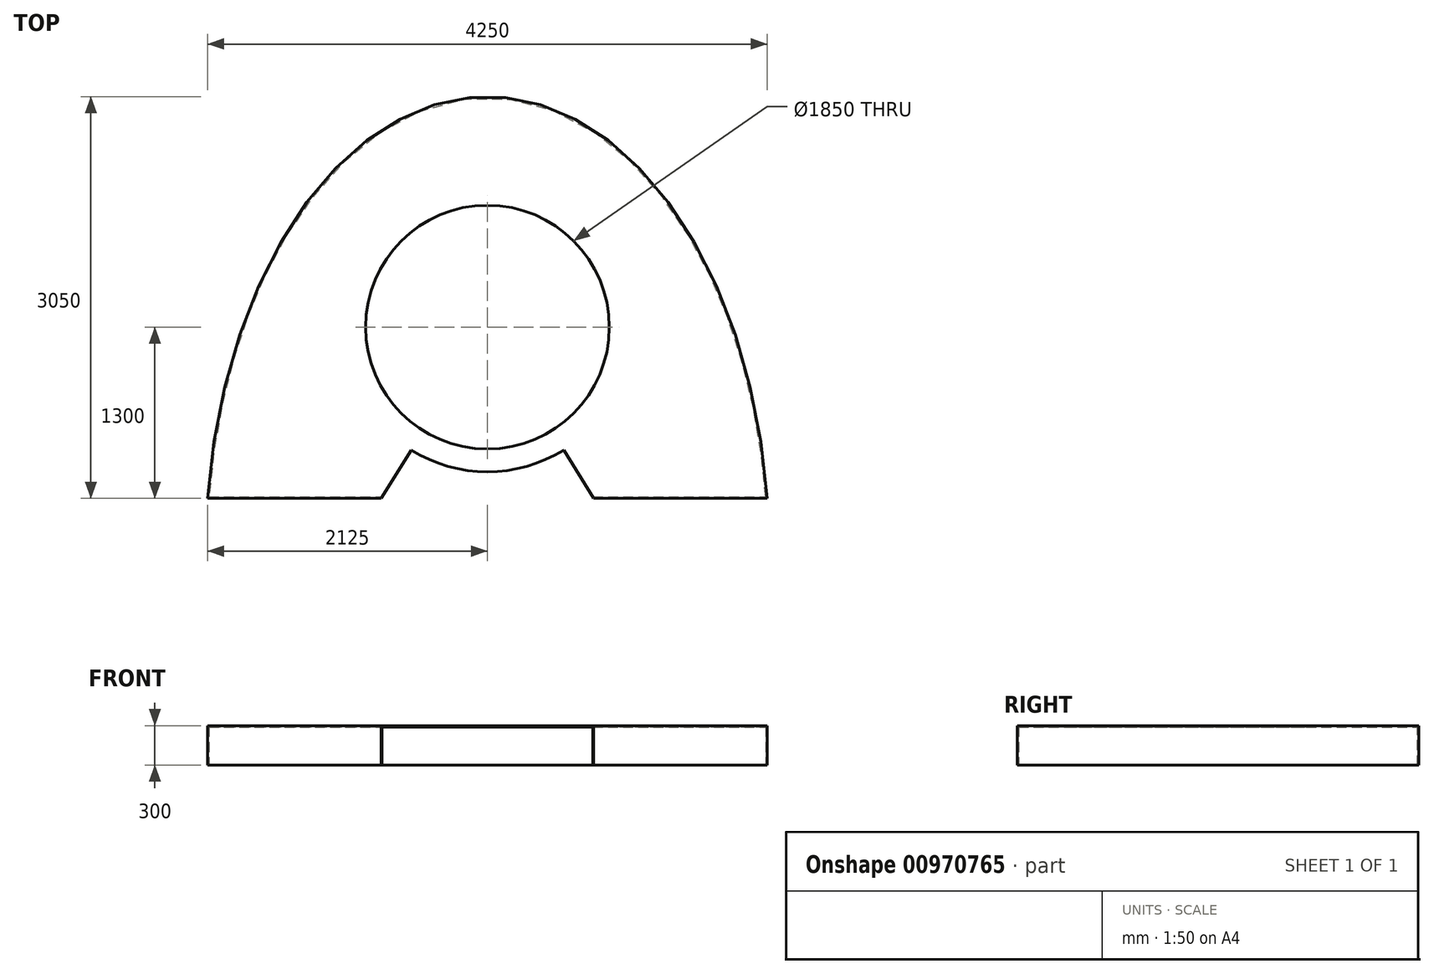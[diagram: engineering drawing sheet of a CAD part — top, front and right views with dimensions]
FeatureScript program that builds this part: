
annotation { "Feature Type Name" : "Feature", "Feature Type Description" : "" }
export const myFeature = defineFeature(function(context is Context, id is Id, definition is map)
    precondition{}
    {
        {
            var Q0;
            Q0=qCreatedBy(makeId("Top.planeOp"),FACE);
            var sketch = newSketch(context, id + "F0", { "sketchPlane" : qUnion([Q0])});
            skLineSegment(sketch, "E0.top", {"start": v(-2125, -1524.96) * mm, "end": v(2125, -1524.96) * mm});
            skEllipticalArc(sketch, "E1", {});
            skPoint(sketch, "E0.left.start.orphan", {"position": v(-2125, 1525.04) * mm});
            skPoint(sketch, "E0.right.start.orphan", {"position": v(2125, 1525.04) * mm});
            skCircle(sketch, "E2", {"center": v(0, -224.96) * mm, "radius": 925 * mm});
            skLineSegment(sketch, "E3", {"start": v(0, -1524.96) * mm, "end": v(-807.5, -1524.96) * mm});
            skLineSegment(sketch, "E4", {"start": v(-807.5, -1524.96) * mm, "end": v(-579.5, -1157.9) * mm});
            skLineSegment(sketch, "E5.MirrorCS", {"start": v(807.5, -1524.96) * mm, "end": v(579.5, -1157.9) * mm});
            skLineSegment(sketch, "E6", {"start": v(807.5, -1524.96) * mm, "end": v(0, -1524.96) * mm});
            skArc(sketch, "E7", {"start": v(-579.5, -1157.9) * mm, "mid": v(0, -1323.23) * mm, "end": v(579.5, -1157.9) * mm});
            skLineSegment(sketch, "E8", {"start": v(-2125, 1525.04) * mm, "end": v(2125, 1525.04) * mm});
            const initialGuessF0  = {"E1": [0, -1.9284895658493042, 0, 1, 3.4535335692987585, 2.1396566964079726, 4.829503089150137, 1.4536822180294497]};
            skSetInitialGuess(sketch, initialGuessF0);
            skSolve(sketch);
        }
        {
            var Q0;
            Q0=makeQuery(id+"F0.imprint","IMPRINT",FACE,{"disambiguationData":[TD([[makeQuery(id+"F0.imprint","IMPRINT",EDGE,{"derivedFrom":sQuery(id+"F0.wireOp",EDGE,"E0.top")}),1.0]])]});
            extrude(context, id + "F1", {"entities" : qUnion([Q0]), "depth" : 300 * mm, "offsetDistance" : 25 * mm});
        }
        {
            var Q0;
            Q0=makeQuery(id+"F1.opExtrude","CAP_FACE",FACE,{"disambiguationData":[OSD([sQuery(id+"F0.wireOp",EDGE,"E0.top"),sQuery(id+"F0.wireOp",EDGE,"E1"),sQuery(id+"F0.wireOp",EDGE,"E2"),sQuery(id+"F0.wireOp",EDGE,"E4"),sQuery(id+"F0.wireOp",EDGE,"E5.MirrorCS"),sQuery(id+"F0.wireOp",EDGE,"E7")])],"isStart":true});
            var Q1;
            Q1=makeQuery(id+"F1.opExtrude","SWEPT_FACE",FACE,{"disambiguationData":[OSD([sQuery(id+"F0.wireOp",EDGE,"E7")])]});
            var Q2;
            Q2=makeQuery(id+"F1.opExtrude","SWEPT_FACE",FACE,{"disambiguationData":[OSD([sQuery(id+"F0.wireOp",EDGE,"E4")])]});
            var Q3;
            {var subQ0=sQuery(id+"F0.wireOp",EDGE,"E0.top");Q3=makeQuery(id+"F1.opExtrude","SWEPT_FACE",FACE,{"disambiguationData":[OSD([subQ0]),TDD([makeQuery(id+"F0.imprint","IMPRINT",EDGE,{"disambiguationData":[TD([[makeQuery(id+"F0.imprint","INTERSECT",VERTEX,{"disambiguationData":[OD(0.0)],"derivedFrom":[subQ0,sQuery(id+"F0.wireOp",EDGE,"E1")]}),-1.0]])],"derivedFrom":subQ0})])]});}
            var Q4;
            {var subQ0=sQuery(id+"F0.wireOp",EDGE,"E0.top");Q4=makeQuery(id+"F1.opExtrude","SWEPT_FACE",FACE,{"disambiguationData":[OSD([subQ0]),TDD([makeQuery(id+"F0.imprint","IMPRINT",EDGE,{"disambiguationData":[TD([[makeQuery(id+"F0.imprint","INTERSECT",VERTEX,{"disambiguationData":[OD(1.0)],"derivedFrom":[subQ0,sQuery(id+"F0.wireOp",EDGE,"E1")]}),1.0]])],"derivedFrom":subQ0})])]});}
            var Q5;
            Q5=makeQuery(id+"F1.opExtrude","SWEPT_FACE",FACE,{"disambiguationData":[OSD([sQuery(id+"F0.wireOp",EDGE,"E5.MirrorCS")])]});
            var Q6;
            Q6=makeQuery(id+"F1.opExtrude","SWEPT_FACE",FACE,{"disambiguationData":[OSD([sQuery(id+"F0.wireOp",EDGE,"E2")])]});
            shell(context, id + "F2", {"entities" : qUnion([Q0, Q1, Q2, Q3, Q4, Q5, Q6]), "thickness" : 10 * mm});
        }
    });
